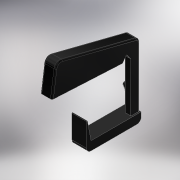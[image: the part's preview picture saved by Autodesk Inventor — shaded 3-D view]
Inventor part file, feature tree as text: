
AUTODESK INVENTOR PART (.ipt)
format: ipt  version: 2018 (Build 220112000, 112)  size: 286,720 bytes
history: native  units: mm
features: extrude x6, fillet x6, other x3, draft x1, chamfer x1
ambient origin geometry x8: Origin, YZ Plane, XZ Plane, XY Plane, X Axis, Y Axis, Z Axis, Center Point
bodies: Solid1 (feature_tree)
feature tree (17):
  extrude  "Key"  Depth=11.0mm
  other  "Hinge Cut Sketch"
  extrude  "Hinge Cut"  TaperAngle=0.0deg  [1 undecoded]
  extrude  "Hinge Cut 2"  Depth=14.835299mm
  other  "Lever Sketch"
  extrude  "Vertical Lever"  Depth=1.0mm
  extrude  "Horizontal Lever"  Depth=10.0mm TaperAngle=0.0deg
  fillet  "Fillet4"  Radius=3.0mm
  fillet  "Fillet5"  Radius=3.0mm
  fillet  "Fillet6"  Radius=33.6625mm
  extrude  "Extrusion12"  Depth=0.5mm
  draft  "FaceDraft3"
  chamfer  "Chamfer1"  Distance=3.0mm
  fillet  "Fillet9"  Radius=6.0mm
  fillet  "Fillet10"  Radius=4.0mm
  fillet  "Fillet11"  Radius=10.0mm
  other  "Key Sketch"
note: 1 required parameter value undecoded (feature->parameter linkage not recoverable at this tier; creation-order binding heuristic only, values carry confidence <= 0.55)
